# Revit family: SW4120
name_source: partatom
category: Plumbing Fixtures
units: mm (PartAtom-declared; Revit-internal decimal feet)

## family parameters
Cut with Voids When Loaded = No
Host = Face
Maintain Annotation Orientation = No
OmniClass Number = 23.45.05.14.14
OmniClass Title = Sinks/Lavatories
Part Type = Normal
Room Calculation Point = No
Round Connector Dimension = Use Diameter
Shared = Yes

## types (2) — shared parameters
Assembly Code = D2010310
CW Connection = No
CWFU = 1.5
Deck Height = 34"
Default Elevation = 0"
Description = One-Station Wash-Ware Eco-Trough Stainless Steel Trough Sink
EG10 Enviro-Glaze Color (White) = No
Faucet Hole Distance = 4"
Finish = Stainless_Steel-Acorn-Satin
Flow Rate = 0.5 GPM (1.9 LPM)
HW Connection = No
HWFU = 1.5
Height = 6 1/2"
IAPMO Compliance = Uniform Plumbing Code (UPC ), ® National Plumbing Code of Canada (cUPC ) and ASME A112.19.3.
Installation Instruction Link = https://www.acorneng.com
Installation Type = Wall Mounted
Length = 16"
Manufacturer = Acorn Engineering
Material = Stainless_Steel-Acorn-Satin
Optional 1-1/2” Tail piece & P-trap = Yes
Product Documentation Link = https://www.acorneng.com
Product Page URL = https://www.acorneng.com
SW000-24   Front Support Legs, 24” Rim Height (Child) = No
SW000-30   Front Support Legs, 30” Rim Height (Junior) = No
SW000-34 Front Support Legs, 34” Rim Height (Adult) = No
SW000-F50 H&C Wristblade Faucet, Gooseneck Spout = No
SW000-F51 H&C Wristblade Faucet, Spout = No
SW000-F60 S/T Sensor Operated Faucet, J Spout, Plate = No
SW000-F70 S/T Pushbutton Metering Faucet, Plate = No
SW000-PT   Daisy Strainer, Tailpiece, 1-1/2” P-Trap, Plastic = No
SW000-PTC Daisy Strainer, Tailpiece, 1-1/2” P-Trap, Chrome = No
SW000-SG   Splash Guard, (Multi-Station Units) = No
URL = http://www.acorneng.com
Vent Connection = No
WFU = 2
WH-DECAL  10” Sticky Decal “Wash Your Hands” = No
Waste Connection = Yes
Waste Connection Diameter = 1 1/2"
Width = 120"

## type names (no varying parameters)
- SW4120-34
- SW4120-4LF4120-34

note: column(s) folded — value = type name in every type: Model

## geometry (parser evidence)
native form markers: Sweep x2
no freeform markers — native parametric forms only
